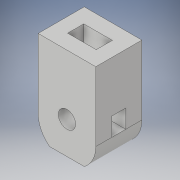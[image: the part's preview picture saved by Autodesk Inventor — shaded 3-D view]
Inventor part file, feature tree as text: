
AUTODESK INVENTOR PART (.ipt)
format: ipt  version: 2019 (Build 230136000, 136)  size: 161,792 bytes
history: native  units: mm
features: sketch x8, extrude x5, plane x1, hole x1, projected_geometry x1
ambient origin geometry x8: Origin, YZ Plane, XZ Plane, XY Plane, X Axis, Y Axis, Z Axis, Center Point
bodies: Solid1 (feature_tree)
feature tree (16):
  extrude  "Extrusion1"  Depth=30.0mm
  plane  "Work Plane1"
  extrude  "Extrusion2"  Depth=12.5mm
  sketch  "Sketch3"  dims[d4=12.5mm d5=12.5mm]
  sketch  "Sketch4"  dims[d6=20.0mm d7=0.0mm d8=10.0mm]
  extrude  "Extrusion3"  Depth=12.5mm
  hole  "Hole1"  [1 undecoded]
  extrude  "Extrusion4"  Depth=7.0mm TaperAngle=0.0deg
  extrude  "Extrusion5"  Depth=6.0mm
  sketch  "Sketch1"  dims[d0=25.0mm d1=30.0mm]
  sketch  "Sketch2"  dims[d2=30.0mm d3=12.5mm]
  projected_geometry  "Projected Loop1"
  sketch  "Sketch6"  dims[d9=12.4mm d10=7.0mm d11=0.0mm]
  sketch  "Sketch7"  dims[d12=30.0mm d13=0.0mm]
  sketch  "Sketch8"  dims[d14=7.5mm d15=6.0mm d16=4.0mm d17=2.0mm d18=90.0deg d19=8.0mm d20=0.0mm d21=6.0mm]
  sketch  "Sketch9"  dims[d22=8.0mm d23=7.0mm d24=0.0mm d25=25.0mm d26=0.0mm d27=26.0mm d28=12.5mm d29=10.0mm d30=5.0mm d31=20.0mm d32=20.0mm d33=0.0mm]
note: 1 required parameter value undecoded (feature->parameter linkage not recoverable at this tier; creation-order binding heuristic only, values carry confidence <= 0.55)
